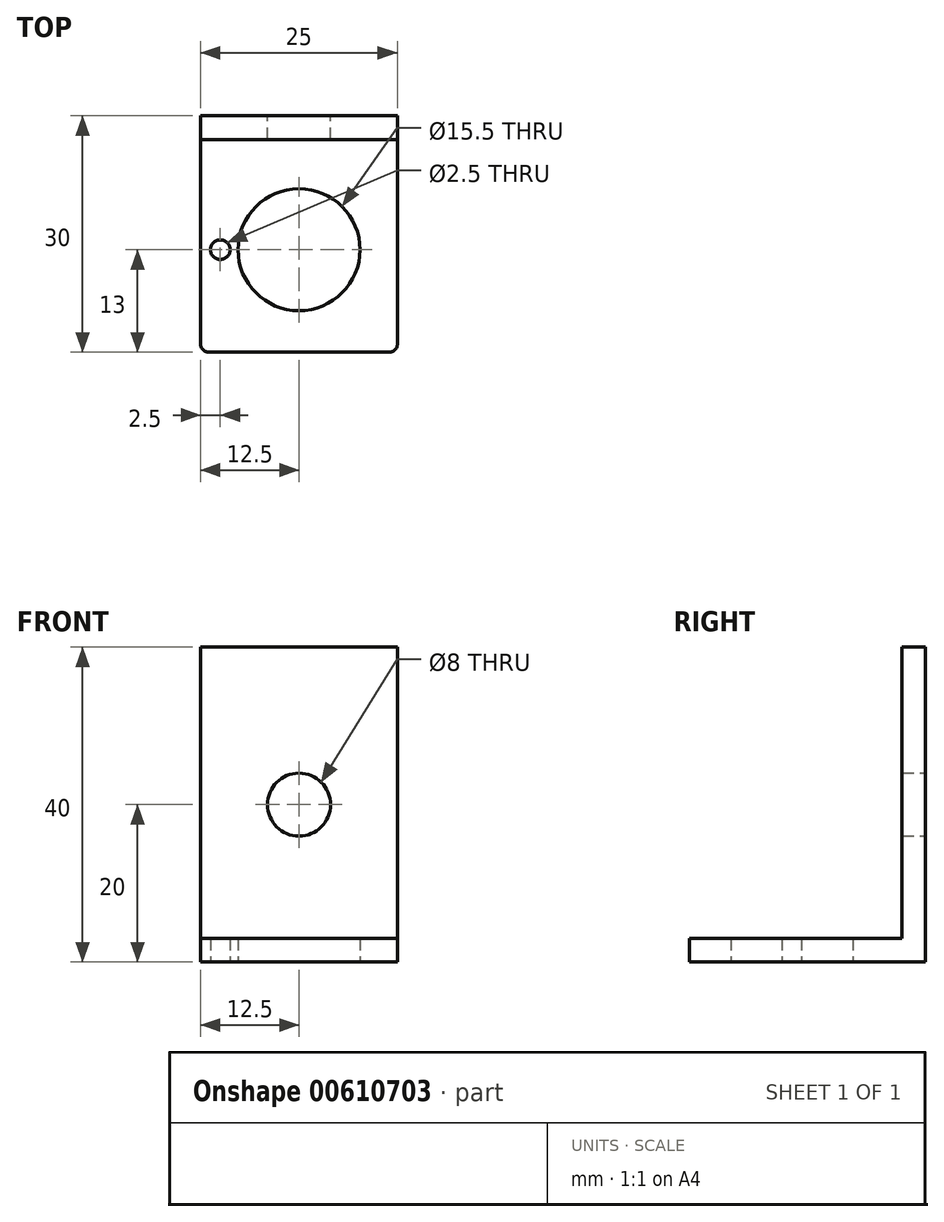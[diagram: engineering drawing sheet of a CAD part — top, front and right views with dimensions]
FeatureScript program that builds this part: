
annotation { "Feature Type Name" : "Feature", "Feature Type Description" : "" }
export const myFeature = defineFeature(function(context is Context, id is Id, definition is map)
    precondition{}
    {
        {
            var Q0;
            Q0=qCreatedBy(makeId("Top.planeOp"),FACE);
            var sketch = newSketch(context, id + "F0", { "sketchPlane" : qUnion([Q0])});
            skLineSegment(sketch, "E0.bottom", {"start": v(-12.5, 15) * mm, "end": v(12.5, 15) * mm});
            skLineSegment(sketch, "E0.top", {"start": v(-12.5, -15) * mm, "end": v(12.5, -15) * mm});
            skLineSegment(sketch, "E0.left", {"start": v(-12.5, 15) * mm, "end": v(-12.5, -15) * mm});
            skLineSegment(sketch, "E0.right", {"start": v(12.5, 15) * mm, "end": v(12.5, -15) * mm});
            skPoint(sketch, "E0.middle", {"position": v(0, 0) * mm});
            skCircle(sketch, "E1", {"center": v(0, -2) * mm, "radius": 7.75 * mm});
            skCircle(sketch, "E2", {"center": v(-10, -2) * mm, "radius": 1.25 * mm});
            skLineSegment(sketch, "E3.top", {"start": v(-12.5, 12) * mm, "end": v(12.5, 12) * mm});
            skLineSegment(sketch, "E3.left", {"start": v(-12.5, 15) * mm, "end": v(-12.5, 12) * mm});
            skLineSegment(sketch, "E3.right", {"start": v(12.5, 15) * mm, "end": v(12.5, 12) * mm});
            skSolve(sketch);
        }
        {
            var Q0;
            Q0=makeQuery(id+"F0.imprint","IMPRINT",FACE,{"disambiguationData":[TD([[makeQuery(id+"F0.imprint","IMPRINT",EDGE,{"derivedFrom":sQuery(id+"F0.wireOp",EDGE,"E0.top")}),1.0]])]});
            extrude(context, id + "F1", {"entities" : qUnion([Q0]), "depth" : 3 * mm, "offsetDistance" : 25 * mm});
        }
        {
            var Q0;
            Q0=makeQuery(id+"F0.imprint","IMPRINT",FACE,{"disambiguationData":[TD([[makeQuery(id+"F0.imprint","IMPRINT",EDGE,{"derivedFrom":sQuery(id+"F0.wireOp",EDGE,"E0.bottom")}),-1.0]])]});
            extrude(context, id + "F2", {"entities" : qUnion([Q0]), "operationType" : NewBodyOperationType.ADD, "depth" : 40 * mm, "offsetDistance" : 25 * mm});
        }
        {
            var Q0;
            Q0=makeQuery(id+"F2.opExtrude","SWEPT_FACE",FACE,{"disambiguationData":[OSD([sQuery(id+"F0.wireOp",EDGE,"E0.bottom")])]});
            var sketch = newSketch(context, id + "F3", { "sketchPlane" : qUnion([Q0])});
            skCircle(sketch, "E4", {"center": v(0, 20) * mm, "radius": 4 * mm});
            skPoint(sketch, "E4.centerSnap0", {"position": v(12.5, 20) * mm});
            skSolve(sketch);
        }
        {
            var Q0;
            Q0=makeQuery(id+"F3.imprint","IMPRINT",FACE,{"disambiguationData":[TD([[makeQuery(id+"F3.imprint","IMPRINT",EDGE,{"derivedFrom":sQuery(id+"F3.wireOp",EDGE,"E4")}),1.0]])]});
            extrude(context, id + "F4", {"entities" : qUnion([Q0]), "operationType" : NewBodyOperationType.REMOVE, "oppositeDirection" : true, "depth" : 25 * mm, "offsetDistance" : 25 * mm});
        }
        {
            var Q0;
            Q0=makeQuery(id+"F1.opExtrude","SWEPT_EDGE",EDGE,{"disambiguationData":[OSD([sQuery(id+"F0.wireOp",EDGE,"E0.top"),sQuery(id+"F0.wireOp",EDGE,"E0.right")])]});
            var Q1;
            Q1=makeQuery(id+"F1.opExtrude","SWEPT_EDGE",EDGE,{"disambiguationData":[OSD([sQuery(id+"F0.wireOp",EDGE,"E0.top"),sQuery(id+"F0.wireOp",EDGE,"E0.left")])]});
            fillet(context, id + "F5", {"entities" : qUnion([Q0, Q1]), "radius" : 1 * mm, "tangentPropagation" : true, "allowEdgeOverflow" : false});
        }
    });
